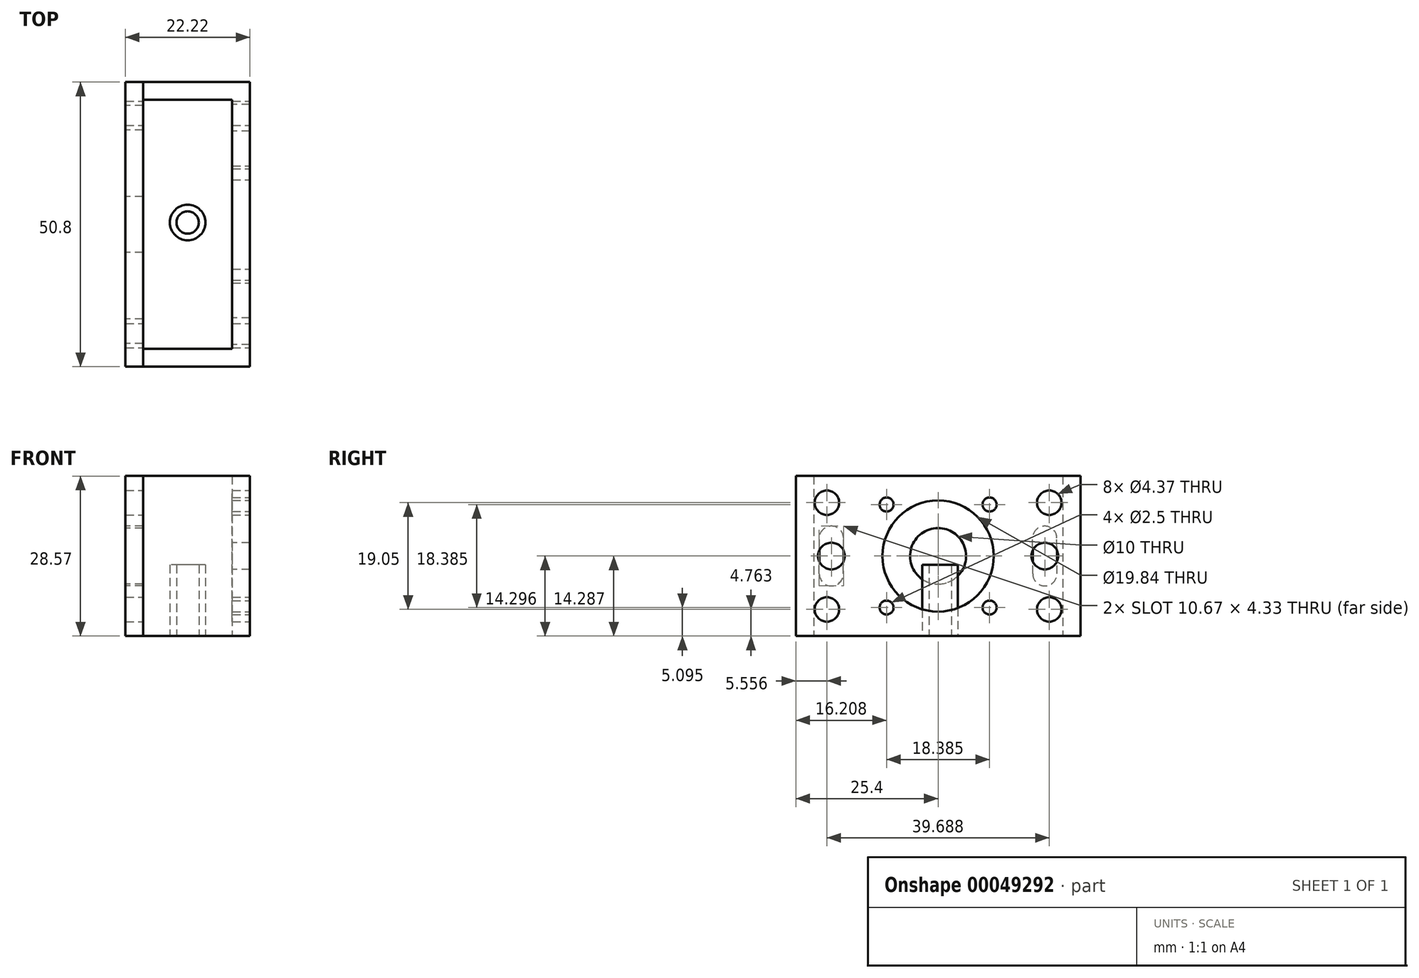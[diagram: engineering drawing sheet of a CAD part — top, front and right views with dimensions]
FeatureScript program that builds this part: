
annotation { "Feature Type Name" : "Feature", "Feature Type Description" : "" }
export const myFeature = defineFeature(function(context is Context, id is Id, definition is map)
    precondition{}
    {
        {
            var Q0;
            Q0=qCreatedBy(makeId("Top.planeOp"),FACE);
            var sketch = newSketch(context, id + "F0", { "sketchPlane" : qUnion([Q0])});
            skCircle(sketch, "E0", {"center": v(0, 0.35) * mm, "radius": 3.18 * mm});
            skCircle(sketch, "E1", {"center": v(0, 0.35) * mm, "radius": 2 * mm});
            skSolve(sketch);
        }
        {
            var Q0;
            Q0=qSketchRegion(id+"F0",true);
            extrude(context, id + "F1", {"entities" : qUnion([Q0]), "depth" : 12.7 * mm});
        }
        {
            var Q0;
            Q0=qCreatedBy(makeId("Top.planeOp"),FACE);
            var sketch = newSketch(context, id + "F2", { "sketchPlane" : qUnion([Q0])});
            skLineSegment(sketch, "E2.rect.bottom", {"start": v(7.94, 22.22) * mm, "end": v(-7.94, 22.22) * mm});
            skLineSegment(sketch, "E2.rect.top", {"start": v(7.94, -22.22) * mm, "end": v(-7.94, -22.22) * mm});
            skLineSegment(sketch, "E2.rect.left", {"start": v(7.94, 22.22) * mm, "end": v(7.94, -22.23) * mm});
            skPoint(sketch, "E2.rect.middle", {"position": v(0, 0) * mm});
            skLineSegment(sketch, "E3.0", {"start": v(11.11, 25.4) * mm, "end": v(-7.94, 25.4) * mm});
            skLineSegment(sketch, "E3.1", {"start": v(11.11, 25.4) * mm, "end": v(11.11, -25.4) * mm});
            skLineSegment(sketch, "E3.2", {"start": v(11.11, -25.4) * mm, "end": v(-7.94, -25.4) * mm});
            skLineSegment(sketch, "E4", {"start": v(-7.94, 22.22) * mm, "end": v(-7.94, 25.4) * mm});
            skLineSegment(sketch, "E5", {"start": v(-7.94, -22.22) * mm, "end": v(-7.94, -25.4) * mm});
            skSolve(sketch);
        }
        {
            var Q0;
            Q0=qSketchRegion(id+"F2",true);
            extrude(context, id + "F3", {"entities" : qUnion([Q0]), "depth" : 28.57 * mm});
        }
        {
            var Q0;
            Q0=makeQuery(id+"F3.opExtrude","SWEPT_FACE",FACE,{"disambiguationData":[OSD([sQuery(id+"F2.wireOp",EDGE,"E3.1")])]});
            var sketch = newSketch(context, id + "F4", { "sketchPlane" : qUnion([Q0])});
            skLineSegment(sketch, "E6", {"start": v(25.4, 14.29) * mm, "end": v(-25.4, 14.29) * mm, "construction": true});
            skLineSegment(sketch, "E7", {"start": v(0, 28.58) * mm, "end": v(0, 0) * mm, "construction": true});
            skCircle(sketch, "E8", {"center": v(0, 14.29) * mm, "radius": 9.92 * mm});
            skCircle(sketch, "E9", {"center": v(0, 14.29) * mm, "radius": 13 * mm, "construction": true});
            skCircle(sketch, "E10", {"center": v(9.2, 23.48) * mm, "radius": 1.25 * mm});
            skLineSegment(sketch, "E11", {"start": v(9.2, 23.48) * mm, "end": v(0, 14.29) * mm, "construction": true});
            skCircle(sketch, "E12.1.0", {"center": v(-9.2, 23.48) * mm, "radius": 1.25 * mm});
            skCircle(sketch, "E12.2.0", {"center": v(-9.2, 5.1) * mm, "radius": 1.25 * mm});
            skCircle(sketch, "E12.3.0", {"center": v(9.2, 5.1) * mm, "radius": 1.25 * mm});
            skSolve(sketch);
        }
        {
            var Q0;
            Q0=qSketchRegion(id+"F4",true);
            extrude(context, id + "F5", {"entities" : qUnion([Q0]), "operationType" : NewBodyOperationType.REMOVE, "endBound" : BoundingType.UP_TO_NEXT, "oppositeDirection" : true, "depth" : 25 * mm});
        }
        {
            var Q0;
            Q0=qCreatedBy(makeId("Top.planeOp"),FACE);
            var sketch = newSketch(context, id + "F6", { "sketchPlane" : qUnion([Q0])});
            skLineSegment(sketch, "E13.bottom", {"start": v(-7.94, 25.4) * mm, "end": v(-11.11, 25.4) * mm});
            skLineSegment(sketch, "E13.top", {"start": v(-7.94, -25.4) * mm, "end": v(-11.11, -25.4) * mm});
            skLineSegment(sketch, "E13.left", {"start": v(-7.94, 25.4) * mm, "end": v(-7.94, -25.4) * mm});
            skLineSegment(sketch, "E13.right", {"start": v(-11.11, 25.4) * mm, "end": v(-11.11, -25.4) * mm});
            skSolve(sketch);
        }
        {
            var Q0;
            Q0=qSketchRegion(id+"F6",true);
            var Q1;
            Q1=makeQuery(id+"F3.opExtrude","CAP_FACE",FACE,{"disambiguationData":[OSD([sQuery(id+"F2.wireOp",EDGE,"E2.rect.bottom"),sQuery(id+"F2.wireOp",EDGE,"E2.rect.top"),sQuery(id+"F2.wireOp",EDGE,"E2.rect.left"),sQuery(id+"F2.wireOp",EDGE,"E3.0"),sQuery(id+"F2.wireOp",EDGE,"E3.1"),sQuery(id+"F2.wireOp",EDGE,"E3.2"),sQuery(id+"F2.wireOp",EDGE,"E4"),sQuery(id+"F2.wireOp",EDGE,"E5")])],"isStart":false});
            extrude(context, id + "F7", {"entities" : qUnion([Q0]), "endBound" : BoundingType.UP_TO_SURFACE, "endBoundEntityFace" : qUnion([Q1]), "depth" : 25.4 * mm});
        }
        {
            var Q0;
            Q0=makeQuery(id+"F7.opExtrude","SWEPT_FACE",FACE,{"disambiguationData":[OSD([sQuery(id+"F6.wireOp",EDGE,"E13.right")])]});
            var sketch = newSketch(context, id + "F8", { "sketchPlane" : qUnion([Q0])});
            skCircle(sketch, "E14", {"center": v(0, 14.29) * mm, "radius": 5 * mm});
            skLineSegment(sketch, "E15", {"start": v(0, 28.57) * mm, "end": v(0, 0) * mm, "construction": true});
            skLineSegment(sketch, "E16", {"start": v(-25.4, 14.29) * mm, "end": v(25.4, 14.29) * mm, "construction": true});
            skSolve(sketch);
        }
        {
            var Q0;
            Q0=qSketchRegion(id+"F8",true);
            extrude(context, id + "F9", {"entities" : qUnion([Q0]), "operationType" : NewBodyOperationType.REMOVE, "endBound" : BoundingType.UP_TO_NEXT, "oppositeDirection" : true, "depth" : 25.4 * mm});
        }
        {
            var Q0;
            Q0=makeQuery(id+"F3.opExtrude","SWEPT_FACE",FACE,{"disambiguationData":[OSD([sQuery(id+"F2.wireOp",EDGE,"E3.1")])]});
            var sketch = newSketch(context, id + "F10", { "sketchPlane" : qUnion([Q0])});
            skLineSegment(sketch, "E17", {"start": v(-19.84, 31.75) * mm, "end": v(-19.84, 0) * mm, "construction": true});
            skPoint(sketch, "E18", {"position": v(-19.84, 23.81) * mm});
            skLineSegment(sketch, "E19", {"start": v(0, 14.29) * mm, "end": v(-25.4, 14.29) * mm, "construction": true});
            skLineSegment(sketch, "E20", {"start": v(0, 14.29) * mm, "end": v(0, 28.57) * mm, "construction": true});
            skPoint(sketch, "E21.MirrorP", {"position": v(-19.84, 4.76) * mm});
            skPoint(sketch, "E22.MirrorP", {"position": v(19.84, 4.76) * mm});
            skPoint(sketch, "E23.MirrorP", {"position": v(19.84, 23.81) * mm});
            skSolve(sketch);
        }
        {
            var Q0;
            Q0=sQuery(id+"F10.wireOp",VERTEX,"E18");
            var Q1;
            Q1=sQuery(id+"F10.wireOp",VERTEX,"E23.MirrorP");
            var Q2;
            Q2=sQuery(id+"F10.wireOp",VERTEX,"E22.MirrorP");
            var Q3;
            Q3=sQuery(id+"F10.wireOp",VERTEX,"E21.MirrorP");
            var Q4;
            Q4=sQuery(id+"F10.wireOp",VERTEX,"7bfd8412-15d2-424a-8f3c-987d5bc530e7");
            var Q5;
            Q5=sQuery(id+"F10.wireOp",VERTEX,"433414ac-6cc2-401e-bdba-70e3e51737870.MirrorP");
            var Q6;
            Q6=makeQuery(id+"F3.opExtrude","SWEPT_BODY",BODY,{"disambiguationData":[OSD([sQuery(id+"F2.wireOp",EDGE,"E2.rect.bottom"),sQuery(id+"F2.wireOp",EDGE,"E2.rect.top"),sQuery(id+"F2.wireOp",EDGE,"E2.rect.left"),sQuery(id+"F2.wireOp",EDGE,"E3.0"),sQuery(id+"F2.wireOp",EDGE,"E3.1"),sQuery(id+"F2.wireOp",EDGE,"E3.2"),sQuery(id+"F2.wireOp",EDGE,"E4"),sQuery(id+"F2.wireOp",EDGE,"E5")])]});
            var Q7;
            Q7=makeQuery(id+"F7.opExtrude","SWEPT_BODY",BODY,{"disambiguationData":[OSD([sQuery(id+"F6.wireOp",EDGE,"E13.bottom"),sQuery(id+"F6.wireOp",EDGE,"E13.top"),sQuery(id+"F6.wireOp",EDGE,"E13.left"),sQuery(id+"F6.wireOp",EDGE,"E13.right")])]});
            hole(context, id + "F11", {"style" : HoleStyle.SIMPLE, "holeDiameter" : 4.37 * mm, "endStyle" : HoleEndStyle.THROUGH, "locations" : qUnion([Q0, Q1, Q2, Q3, Q4, Q5]), "scope" : qUnion([Q6, Q7])});
        }
        {
            var Q0;
            Q0=makeQuery(id+"F7.opExtrude","SWEPT_FACE",FACE,{"disambiguationData":[OSD([sQuery(id+"F6.wireOp",EDGE,"E13.right")])]});
            var sketch = newSketch(context, id + "F12", { "sketchPlane" : qUnion([Q0])});
            skLineSegment(sketch, "E24", {"start": v(-19.05, 26.06) * mm, "end": v(-19.05, 2.53) * mm, "construction": true});
            skLineSegment(sketch, "E25", {"start": v(0, 14.29) * mm, "end": v(0, 21.1) * mm, "construction": true});
            skLineSegment(sketch, "E26.rect.left", {"start": v(-16.9, 11.12) * mm, "end": v(-16.89, 17.47) * mm});
            skLineSegment(sketch, "E26.rect.right", {"start": v(-21.21, 11.12) * mm, "end": v(-21.2, 17.47) * mm});
            skPoint(sketch, "E26.rect.middle", {"position": v(-19.05, 14.3) * mm});
            skArc(sketch, "E27", {"start": v(-16.89, 17.47) * mm, "mid": v(-19.04, 19.63) * mm, "end": v(-21.2, 17.47) * mm});
            skArc(sketch, "E28", {"start": v(-21.21, 11.12) * mm, "mid": v(-19.06, 8.96) * mm, "end": v(-16.9, 11.12) * mm});
            skPoint(sketch, "E29.MirrorP", {"position": v(19.05, 14.3) * mm});
            skLineSegment(sketch, "E30.MirrorCS", {"start": v(21.21, 11.12) * mm, "end": v(21.2, 17.47) * mm});
            skArc(sketch, "E31.MirrorCS", {"start": v(21.21, 11.12) * mm, "mid": v(19.06, 8.96) * mm, "end": v(16.9, 11.12) * mm});
            skLineSegment(sketch, "E32.MirrorCS", {"start": v(16.9, 11.12) * mm, "end": v(16.89, 17.47) * mm});
            skArc(sketch, "E33.MirrorCS", {"start": v(16.89, 17.47) * mm, "mid": v(19.04, 19.63) * mm, "end": v(21.2, 17.47) * mm});
            skSolve(sketch);
        }
        {
            var Q0;
            Q0=qSketchRegion(id+"F12",true);
            extrude(context, id + "F13", {"entities" : qUnion([Q0]), "operationType" : NewBodyOperationType.REMOVE, "endBound" : BoundingType.UP_TO_NEXT, "oppositeDirection" : true, "depth" : 25.4 * mm});
        }
        {
            var Q0;
            Q0=makeQuery(id+"F3.opExtrude","SWEPT_FACE",FACE,{"disambiguationData":[OSD([sQuery(id+"F2.wireOp",EDGE,"E2.rect.left")])]});
            var sketch = newSketch(context, id + "F14", { "sketchPlane" : qUnion([Q0])});
            skLineSegment(sketch, "E34", {"start": v(-21.2, 14.3) * mm, "end": v(-16.9, 14.3) * mm, "construction": true});
            skCircle(sketch, "E35", {"center": v(-19.05, 14.3) * mm, "radius": 2.38 * mm});
            skLineSegment(sketch, "E36", {"start": v(0, 0) * mm, "end": v(0, 28.58) * mm, "construction": true});
            skCircle(sketch, "E37.MirrorC", {"center": v(19.05, 14.3) * mm, "radius": 2.38 * mm});
            skSolve(sketch);
        }
        {
            var Q0;
            Q0=qSketchRegion(id+"F14",true);
            extrude(context, id + "F15", {"entities" : qUnion([Q0]), "operationType" : NewBodyOperationType.REMOVE, "endBound" : BoundingType.UP_TO_NEXT, "oppositeDirection" : true, "depth" : 25 * mm});
        }
    });
